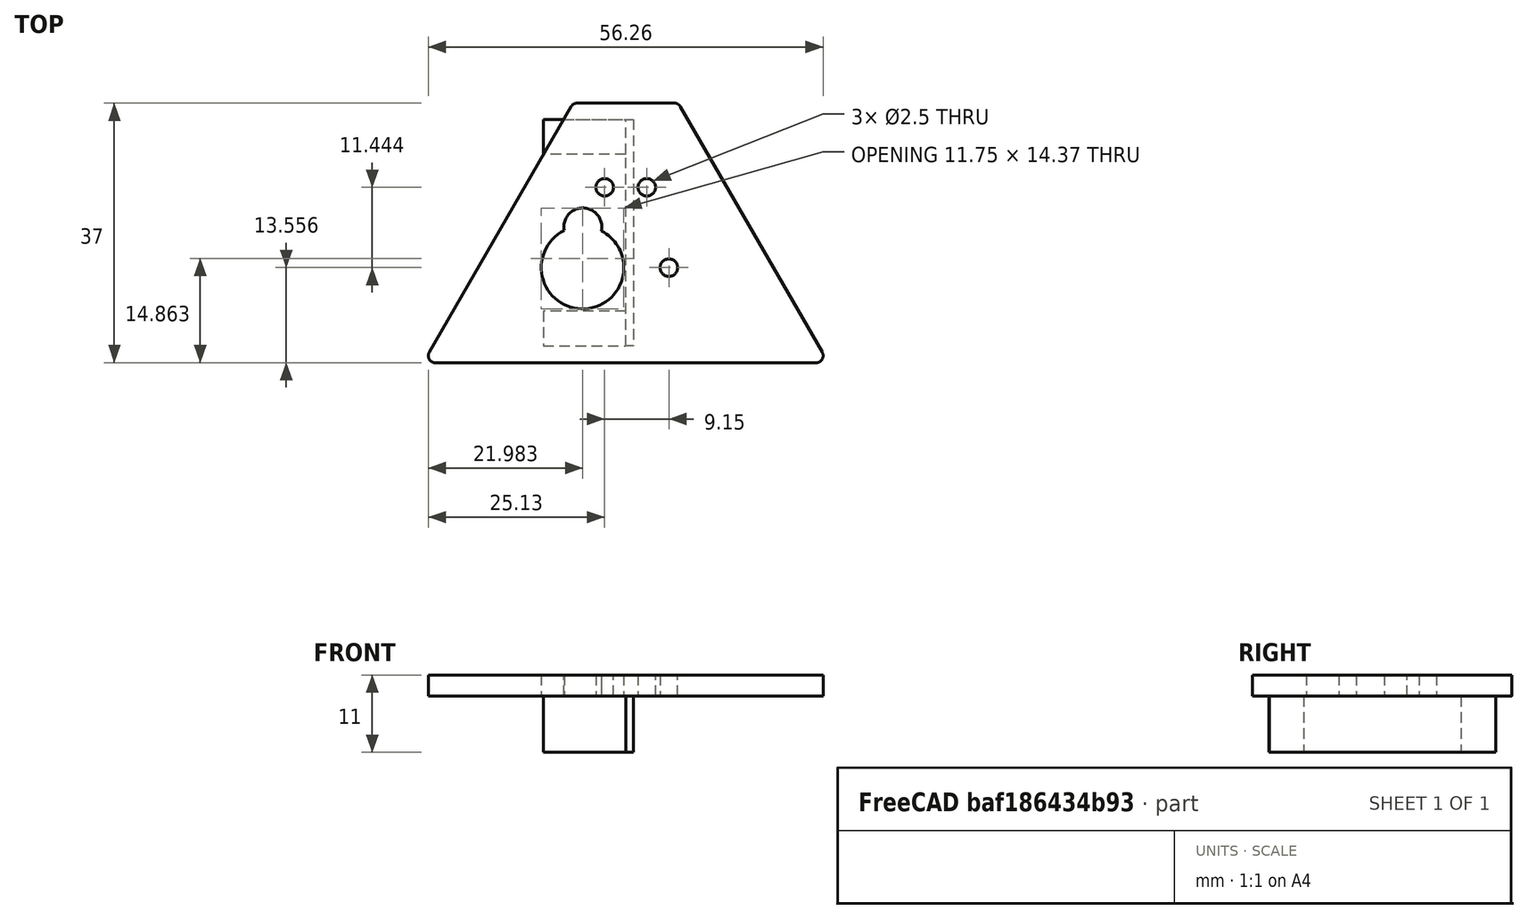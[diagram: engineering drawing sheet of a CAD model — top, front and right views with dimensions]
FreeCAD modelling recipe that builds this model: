
FCSTD DOCUMENT  (FreeCAD 0.20R29410 (Git))
Label: Base
License: All rights reserved
LicenseURL: http://en.wikipedia.org/wiki/All_rights_reserved
objects: Sketcher::SketchObject×3, Part::Extrusion×3, Part::Fillet×1, Part::Cut×1
note: 8 computed .brp shape members not serialized (recipe doc carries the construction recipe); baked Part::Feature solids carry a one-line shape summary decoded from their .brp

FEATURE [Sketcher::SketchObject] Sketch  label="Trapezoid 29.63x10mm with holes r1mm"
  FullyConstrained = false
  sketch-geometry (9):
    g0: LineSegment StartX=0 StartY=0 StartZ=0 EndX=28.862 EndY=0 EndZ=0
    g1: LineSegment StartX=28.862 StartY=0 StartZ=0 EndX=7.5 EndY=37 EndZ=0
    g2: LineSegment StartX=7.5 StartY=37 StartZ=0 EndX=-7.5 EndY=37 EndZ=0
    g3: LineSegment StartX=-28.862 StartY=0 StartZ=0 EndX=0 EndY=0 EndZ=0
    g4: LineSegment StartX=-28.862 StartY=0 StartZ=0 EndX=-7.5 EndY=37 EndZ=0
    g5: Circle CenterX=-3 CenterY=25 CenterZ=0 NormalX=0 NormalY=0 NormalZ=1 AngleXU=0 Radius=1.25
    g6: Circle CenterX=3 CenterY=25 CenterZ=0 NormalX=0 NormalY=0 NormalZ=1 AngleXU=0 Radius=1.25
    g7: Circle CenterX=-6.15 CenterY=13.5556 CenterZ=0 NormalX=0 NormalY=0 NormalZ=1 AngleXU=0 Radius=5.88
    g8: Circle CenterX=6.15 CenterY=13.5556 CenterZ=0 NormalX=0 NormalY=0 NormalZ=1 AngleXU=0 Radius=1.25
  constraints (25):
    c: Coincident(g0,g-1)
    c: PointOnObject(g0,g-1)
    c: Coincident(g1,g0)
    c: Coincident(g2,g1)
    c: Horizontal(g2)
    c: Coincident(g3,g0)
    c: Horizontal(g3)
    c: Angle(g1,g0) = 1.0472
    c: Coincident(g4,g3)
    c: Coincident(g4,g2)
    c: Angle(g3,g4) = 1.0472
    c: DistanceX(g2,g2) = 15
    c: Equal(g0,g3)
    c: Horizontal(g7,g8)
    c: Horizontal(g5,g6)
    c: Equal(g6,g5)
    c: Radius(g5) = 1.25
    c: DistanceY(g0,g1) = 37
    c: DistanceX(g5,g6) = 6
    c: DistanceX(g7,g8) = 12.3
    c: DistanceX(g7,g0) = 6.15
    c: Equal(g6,g8)
    c: Radius(g7) = 5.88
    c: DistanceX(g2,g5) = 4.5
    c: Distance(g6,g8) = 11.87
FEATURE [Part::Extrusion] Extrude  label="Extrusion 3mm"
  Base = -> Sketch
  Dir = (0,0,1)
  DirMode = 2
  FaceMakerClass = Part::FaceMakerBullseye
  LengthFwd = 3
  LengthRev = 0
  Solid = true
  Symmetric = false
FEATURE [Part::Fillet] Fillet  label="Fillet r1mm"
  Base = -> Extrude
  Edges = 4 edges r=1: [Edge2,Edge5,Edge8,Edge11]
FEATURE [Sketcher::SketchObject] Sketch001
  FullyConstrained = false
  MapMode = 5
  Placement = pos=(0,0,3) rot=(0,0,1;0rad)
  Support = -> [Fillet]
  sketch-geometry (1):
    g0: Circle CenterX=-6.10943 CenterY=19.3628 CenterZ=0 NormalX=0 NormalY=0 NormalZ=1 AngleXU=0 Radius=2.7
  constraints (1):
    c: Radius(g0) = 2.7
FEATURE [Part::Extrusion] Extrude001
  Base = -> Sketch001
  Dir = (0,0,1)
  DirMode = 2
  FaceMakerClass = Part::FaceMakerBullseye
  LengthFwd = 10
  LengthRev = 0
  Reversed = true
  Solid = true
  Symmetric = false
FEATURE [Part::Cut] Cut
  Base = -> Fillet
  Refine = true
  Tool = -> Extrude001
FEATURE [Sketcher::SketchObject] Sketch002
  FullyConstrained = false
  MapMode = 5
  Placement = pos=(0,0,0) rot=(1,0,0;3.14159rad)
  Support = -> [Cut]
  sketch-geometry (12):
    g0: LineSegment StartX=-11.75 StartY=-2.39 StartZ=0 EndX=0 EndY=-2.39 EndZ=0
    g1: LineSegment StartX=0 StartY=-2.39 StartZ=0 EndX=0 EndY=-7.34 EndZ=0
    g2: LineSegment StartX=0 StartY=-7.34 StartZ=0 EndX=-11.75 EndY=-7.34 EndZ=0
    g3: LineSegment StartX=-11.75 StartY=-7.34 StartZ=0 EndX=-11.75 EndY=-2.39 EndZ=0
    g4: LineSegment StartX=-11.75 StartY=-34.69 StartZ=0 EndX=0 EndY=-34.69 EndZ=0
    g5: LineSegment StartX=0 StartY=-34.69 StartZ=0 EndX=0 EndY=-29.74 EndZ=0
    g6: LineSegment StartX=0 StartY=-29.74 StartZ=0 EndX=-11.75 EndY=-29.74 EndZ=0
    g7: LineSegment StartX=-11.75 StartY=-29.74 StartZ=0 EndX=-11.75 EndY=-34.69 EndZ=0
    g8: LineSegment StartX=0 StartY=-34.69 StartZ=0 EndX=1.11904 EndY=-34.69 EndZ=0
    g9: LineSegment StartX=1.11904 StartY=-34.69 StartZ=0 EndX=1.11904 EndY=-2.41399 EndZ=0
    g10: LineSegment StartX=1.11904 StartY=-2.41399 StartZ=0 EndX=0 EndY=-2.41399 EndZ=0
    g11: LineSegment StartX=0 StartY=-2.41399 StartZ=0 EndX=0 EndY=-34.69 EndZ=0
  constraints (33):
    c: Coincident(g0,g1)
    c: Coincident(g1,g2)
    c: Coincident(g2,g3)
    c: Coincident(g3,g0)
    c: Horizontal(g0)
    c: Horizontal(g2)
    c: Vertical(g1)
    c: Vertical(g3)
    c: PointOnObject(g1,g-2)
    c: Coincident(g4,g5)
    c: Coincident(g5,g6)
    c: Coincident(g6,g7)
    c: Coincident(g7,g4)
    c: Horizontal(g4)
    c: Horizontal(g6)
    c: Vertical(g5)
    c: Vertical(g7)
    c: DistanceY(g3,g3) = 4.95
    c: DistanceX(g0,g0) = 11.75
    c: Equal(g3,g7)
    c: Equal(g0,g6)
    c: Vertical(g5,g-1)
    c: Coincident(g8,g9)
    c: Coincident(g9,g10)
    c: Coincident(g10,g11)
    c: Coincident(g11,g8)
    c: Horizontal(g8)
    c: Horizontal(g10)
    c: Vertical(g9)
    c: Vertical(g11)
    c: Coincident(g8,g4)
    c: DistanceY(g0,g-1) = 2.39
    c: DistanceY(g5,g1) = 22.4
FEATURE [Part::Extrusion] Extrude002
  Base = -> Sketch002
  Dir = (0,0,-1)
  DirMode = 2
  FaceMakerClass = Part::FaceMakerBullseye
  LengthFwd = 8
  LengthRev = 0
  Solid = true
  Symmetric = false
